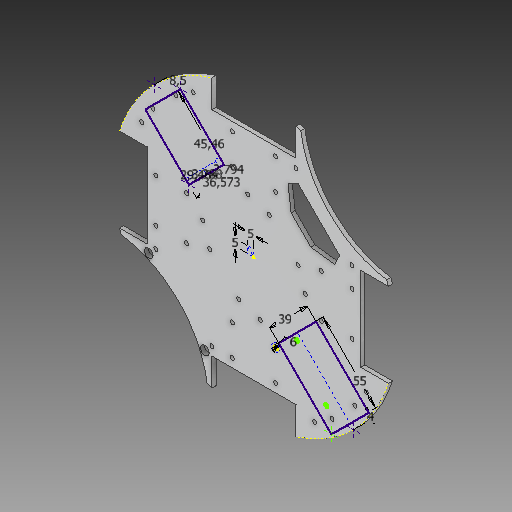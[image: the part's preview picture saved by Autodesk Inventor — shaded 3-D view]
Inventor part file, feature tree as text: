
AUTODESK INVENTOR PART (.ipt)
format: ipt  version: 2020 (Build 240168000, 168)  size: 415,232 bytes
history: native  units: mm
features: sketch x9, extrude x4, hole x4, projected_geometry x2, other x1
ambient origin geometry x8: Origin, YZ Plane, XZ Plane, XY Plane, X Axis, Y Axis, Z Axis, Center Point
bodies: Body1 (feature_tree)
feature tree (20):
  other  "Твердое тело1"
  extrude  "Выдавливание1"  Depth=215.0mm
  extrude  "Выдавливание2"  Depth=208.0mm
  hole  "Отверстие1"  [1 undecoded]
  sketch  "Эскиз10"
  sketch  "Эскиз11"
  extrude  "Выдавливание4"  Depth=31.0mm
  extrude  "Выдавливание5"  Depth=31.0mm
  hole  "Отверстие2"  [1 undecoded]
  hole  "Отверстие3"  [1 undecoded]
  hole  "Отверстие4"  [1 undecoded]
  sketch  "Эскиз2"
  sketch  "Эскиз3"
  sketch  "Эскиз5"
  projected_geometry  "Спроецированная петля2"
  projected_geometry  "Спроецированная петля4"
  sketch  "Эскиз12"
  sketch  "Эскиз14"
  sketch  "Эскиз15"
  sketch  "Эскиз16"
note: 4 required parameter values undecoded (feature->parameter linkage not recoverable at this tier; creation-order binding heuristic only, values carry confidence <= 0.55)
